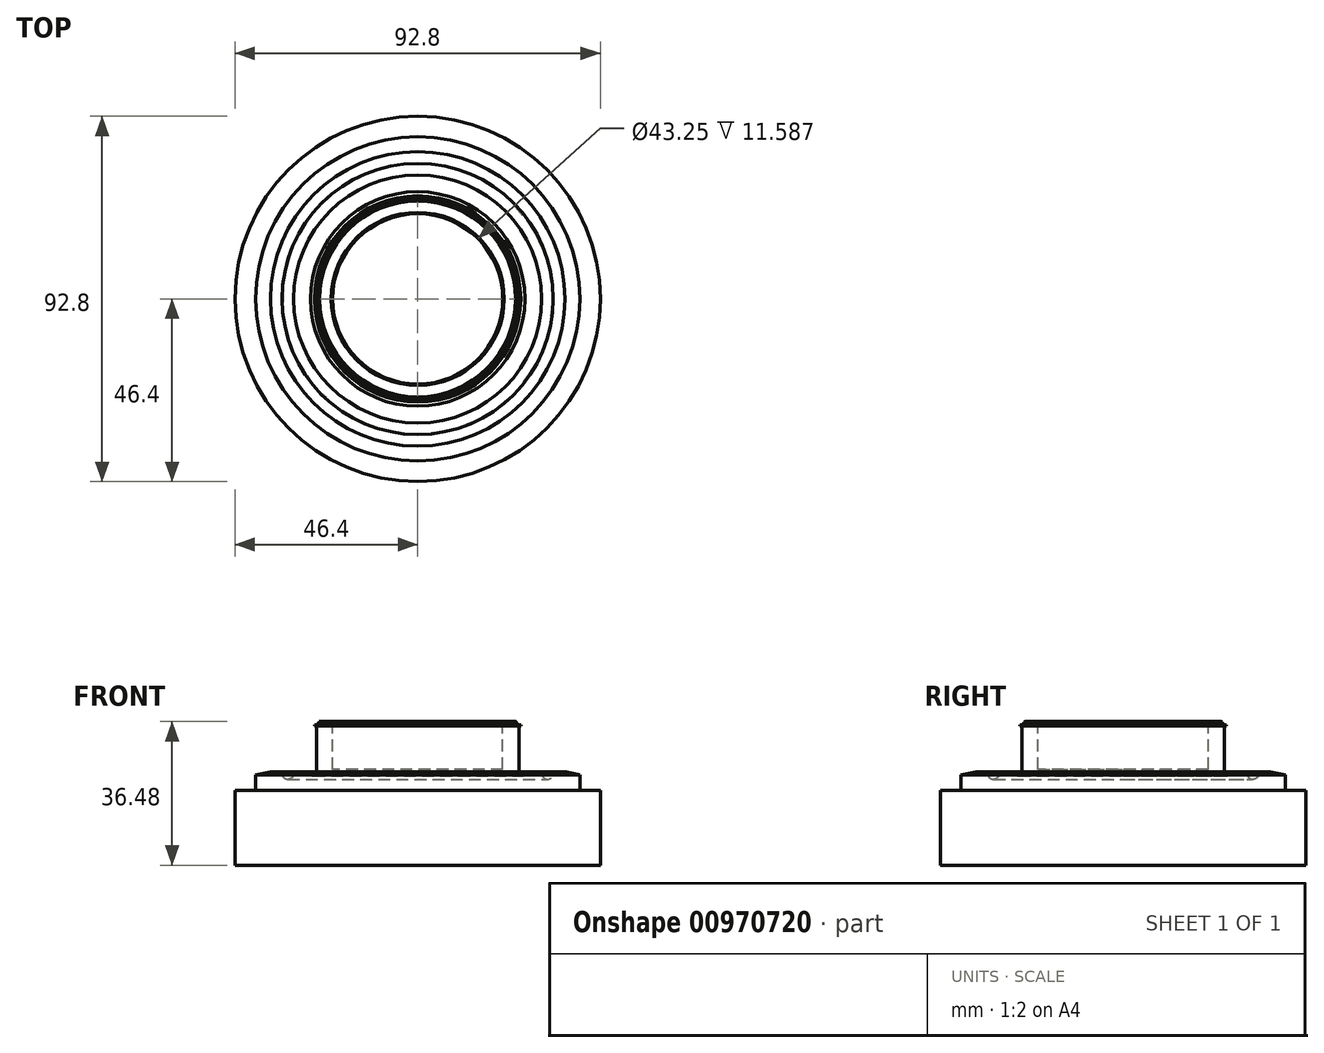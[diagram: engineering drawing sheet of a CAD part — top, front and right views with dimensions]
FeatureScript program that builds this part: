
annotation { "Feature Type Name" : "Feature", "Feature Type Description" : "" }
export const myFeature = defineFeature(function(context is Context, id is Id, definition is map)
    precondition{}
    {
        {
            var Q0;
            Q0=qCreatedBy(makeId("Front.planeOp"),FACE);
            var sketch = newSketch(context, id + "F0", { "sketchPlane" : qUnion([Q0])});
            skLineSegment(sketch, "E0", {"start": v(21.63, 0) * mm, "end": v(24.88, 0) * mm});
            skLineSegment(sketch, "E1", {"start": v(25.7, -0.82) * mm, "end": v(25.7, -12.83) * mm});
            skLineSegment(sketch, "E2", {"start": v(27.23, -13.33) * mm, "end": v(31.51, -13.33) * mm});
            skPoint(sketch, "E3.orphan", {"position": v(0, -13.33) * mm});
            skLineSegment(sketch, "E4", {"start": v(21.63, 0) * mm, "end": v(21.63, -11.94) * mm});
            skArc(sketch, "E5", {"start": v(25.7, -12.83) * mm, "mid": v(26.1, -13.52) * mm, "end": v(26.9, -13.52) * mm});
            skLineSegment(sketch, "E6", {"start": v(26.9, -13.52) * mm, "end": v(27.23, -13.33) * mm});
            skPoint(sketch, "E7.orphan", {"position": v(25.7, -13.33) * mm});
            skLineSegment(sketch, "E8", {"start": v(31.51, -13.33) * mm, "end": v(31.51, -36.27) * mm});
            skLineSegment(sketch, "E9", {"start": v(65.63, -36.27) * mm, "end": v(-46.46, -36.27) * mm});
            skLineSegment(sketch, "E10", {"start": v(37.41, -36.27) * mm, "end": v(37.41, -12.53) * mm});
            skLineSegment(sketch, "E11", {"start": v(37.41, -12.53) * mm, "end": v(34.44, -12.53) * mm});
            skLineSegment(sketch, "E12", {"start": v(28.06, 0) * mm, "end": v(28.06, -0.65) * mm});
            skLineSegment(sketch, "E13", {"start": v(28.06, -0.65) * mm, "end": v(25.7, -0.65) * mm});
            skLineSegment(sketch, "E14", {"start": v(25.58, -0.53) * mm, "end": v(25.17, -0.12) * mm});
            skLineSegment(sketch, "E15", {"start": v(37.41, -12.53) * mm, "end": v(41.19, -13.33) * mm});
            skLineSegment(sketch, "E16", {"start": v(41.19, -13.33) * mm, "end": v(41.19, -17.3) * mm});
            skLineSegment(sketch, "E17", {"start": v(41.19, -17.3) * mm, "end": v(46.4, -17.3) * mm});
            skLineSegment(sketch, "E18", {"start": v(46.4, -17.3) * mm, "end": v(46.4, -36.27) * mm});
            skArc(sketch, "E19", {"start": v(31.51, -13.33) * mm, "mid": v(33.38, -14.4) * mm, "end": v(34.44, -12.53) * mm});
            skLineSegment(sketch, "E20", {"start": v(21.63, -11.94) * mm, "end": v(0, -11.94) * mm});
            skLineSegment(sketch, "E21", {"start": v(0, -11.94) * mm, "end": v(0, -36.27) * mm});
            skLineSegment(sketch, "E22", {"start": v(25.13, 0.2) * mm, "end": v(21.41, 0.2) * mm});
            skLineSegment(sketch, "E23", {"start": v(25.17, 0.3) * mm, "end": v(21.11, 0.3) * mm});
            skLineSegment(sketch, "E24", {"start": v(25.7, -0.23) * mm, "end": v(25.17, 0.3) * mm});
            skLineSegment(sketch, "E25.trimOffspring", {"start": v(25.1, 0.1) * mm, "end": v(21.45, 0.1) * mm});
            skLineSegment(sketch, "E26", {"start": v(25.7, -0.6) * mm, "end": v(24.9, 0.2) * mm});
            skLineSegment(sketch, "E27.trimOffspring", {"start": v(25.7, -0.37) * mm, "end": v(25.13, 0.2) * mm});
            skLineSegment(sketch, "E28.trimOffspring", {"start": v(25.7, -0.5) * mm, "end": v(25.1, 0.1) * mm});
            skLineSegment(sketch, "E29", {"start": v(25.1, 0.1) * mm, "end": v(25, 0.2) * mm});
            skLineSegment(sketch, "E30", {"start": v(25.7, -0.37) * mm, "end": v(26.05, -0.72) * mm});
            skLineSegment(sketch, "E31", {"start": v(25.7, -0.65) * mm, "end": v(26.2, -0.65) * mm});
            skLineSegment(sketch, "E32", {"start": v(26.2, -0.65) * mm, "end": v(26.2, -0.87) * mm});
            skLineSegment(sketch, "E33", {"start": v(26.05, -0.72) * mm, "end": v(26.2, -0.87) * mm});
            skPoint(sketch, "E34.visualSharp", {"position": v(25.7, -0.65) * mm});
            skArc(sketch, "E34.filletArc", {"start": v(25.7, -0.82) * mm, "mid": v(25.67, -0.66) * mm, "end": v(25.58, -0.53) * mm});
            skPoint(sketch, "E35.visualSharp", {"position": v(25.05, 0) * mm});
            skArc(sketch, "E35.filletArc", {"start": v(25.17, -0.12) * mm, "mid": v(25.04, -0.03) * mm, "end": v(24.88, 0) * mm});
            skSolve(sketch);
        }
        {
            var Q0;
            Q0 = qSketchRegion(id + "F0", true);
            var Q1;
            Q1=sQuery(id+"F0.wireOp",EDGE,"E21");
            revolve(context, id + "F1", {"surfaceOperationType" : NewSurfaceOperationType.NEW, "entities" : qUnion([Q0]), "axis" : qUnion([Q1]), "revolveType" : RevolveType.FULL});
        }
        {
            var Q0;
            Q0=makeQuery(id+"F1.opRevolve","SWEPT_EDGE",EDGE,{"disambiguationData":[OSD([sQuery(id+"F0.wireOp",EDGE,"E0"),sQuery(id+"F0.wireOp",EDGE,"E4")])]});
            chamfer(context, id + "F2", {"entities" : qUnion([Q0]), "width" : 0.35 * mm, "tangentPropagation" : true});
        }
    });
